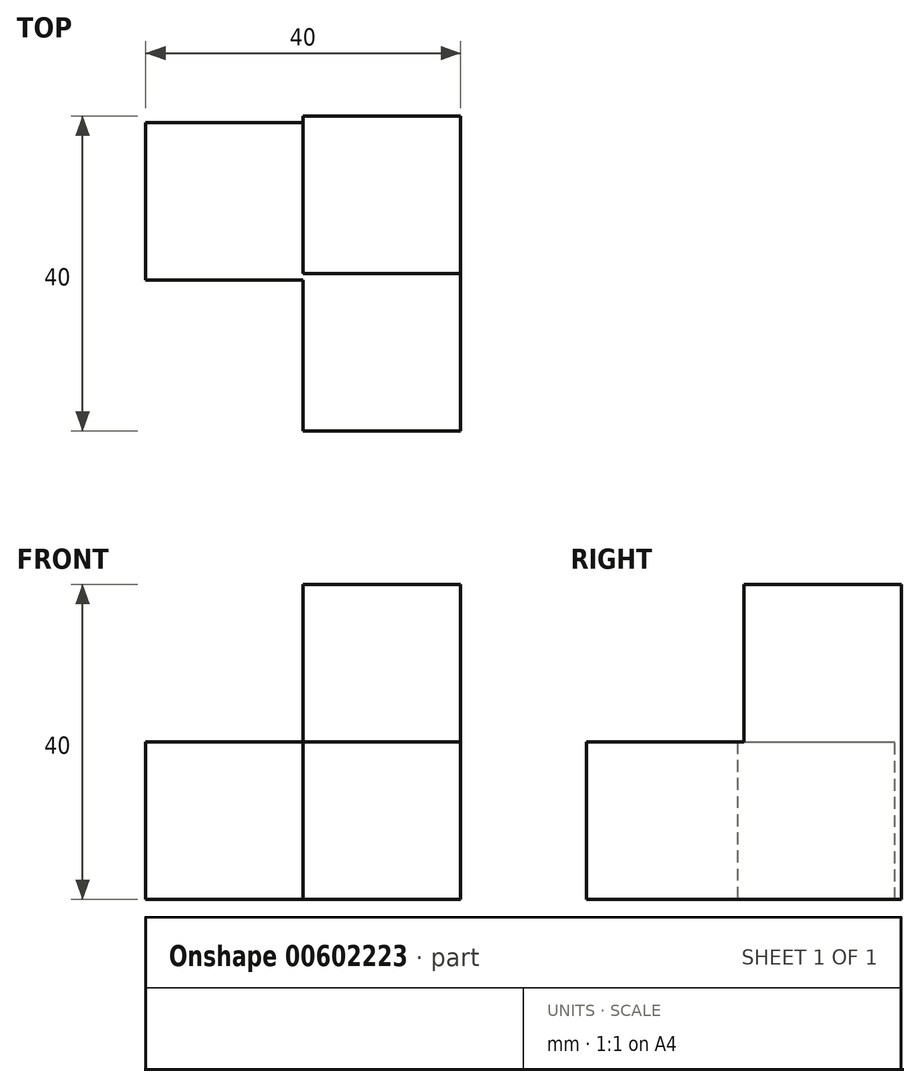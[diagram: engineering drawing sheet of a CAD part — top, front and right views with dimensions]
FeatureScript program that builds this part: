
annotation { "Feature Type Name" : "Feature", "Feature Type Description" : "" }
export const myFeature = defineFeature(function(context is Context, id is Id, definition is map)
    precondition{}
    {
        {
            var Q0;
            Q0=qCreatedBy(makeId("Right.planeOp"),FACE);
            var sketch = newSketch(context, id + "F0", { "sketchPlane" : qUnion([Q0])});
            skLineSegment(sketch, "E0", {"start": v(43.93, 20) * mm, "end": v(43.93, -20) * mm});
            skLineSegment(sketch, "E1", {"start": v(43.93, -20) * mm, "end": v(3.93, -20) * mm});
            skLineSegment(sketch, "E2", {"start": v(3.93, -20) * mm, "end": v(3.93, 0) * mm});
            skLineSegment(sketch, "E3", {"start": v(3.93, 0) * mm, "end": v(23.93, 0) * mm});
            skPoint(sketch, "E3.endSnap0", {"position": v(43.93, 0) * mm});
            skLineSegment(sketch, "E4", {"start": v(43.93, 20) * mm, "end": v(23.93, 20) * mm});
            skLineSegment(sketch, "E5", {"start": v(23.93, 20) * mm, "end": v(23.93, 0) * mm});
            skSolve(sketch);
        }
        {
            var Q0;
            Q0=makeQuery(id+"F0.imprint","IMPRINT",FACE,{"disambiguationData":[TD([[makeQuery(id+"F0.imprint","IMPRINT",EDGE,{"derivedFrom":sQuery(id+"F0.wireOp",EDGE,"E0")}),-1.0]])]});
            extrude(context, id + "F1", {"entities" : qUnion([Q0]), "depth" : 20 * mm, "offsetDistance" : 25 * mm});
        }
        {
            var Q0;
            Q0=qCreatedBy(makeId("Right.planeOp"),FACE);
            var sketch = newSketch(context, id + "F2", { "sketchPlane" : qUnion([Q0])});
            skLineSegment(sketch, "E6", {"start": v(23.1, 0) * mm, "end": v(43.1, 0) * mm});
            skLineSegment(sketch, "E7", {"start": v(23.1, 0) * mm, "end": v(23.1, -20) * mm});
            skLineSegment(sketch, "E8", {"start": v(23.1, -20) * mm, "end": v(43.1, -20) * mm});
            skLineSegment(sketch, "E9", {"start": v(43.1, -20) * mm, "end": v(43.1, 0) * mm});
            skSolve(sketch);
        }
        {
            var Q0;
            Q0=makeQuery(id+"F2.imprint","IMPRINT",FACE,{"disambiguationData":[TD([[makeQuery(id+"F2.imprint","IMPRINT",EDGE,{"derivedFrom":sQuery(id+"F2.wireOp",EDGE,"E6")}),-1.0]])]});
            extrude(context, id + "F3", {"entities" : qUnion([Q0]), "operationType" : NewBodyOperationType.ADD, "oppositeDirection" : true, "depth" : 20 * mm, "offsetDistance" : 25 * mm});
        }
    });
